# Revit family: EC-25-TY9128_Metric
name_source: partatom
category: Sprinklers
units: mm (PartAtom-declared; Revit-internal decimal feet)

## family parameters
Always vertical = Yes
Cut with Voids When Loaded = No
Maintain Annotation Orientation = No
OmniClass Number = 23.65.70.17.11.24
OmniClass Title = Fire Fighting Sprinkler Heads
Part Type = Normal
Room Calculation Point = No
Round Connector Dimension = Use Diameter
Shared = No
Work Plane-Based = No

## types (2) — shared parameters
COBie = Yes
COBie.Component.Name = Sprinklers:ESFR Upright_SIN
COBie.Type = Yes
COBie.Type.AssetType = Fixed
COBie.Type.Category = Pr_70_55_97_84:Sprinklers
COBie.Type.Colour = Yellow
COBie.Type.DurationUnit = year
COBie.Type.Finish = Natural Brass
COBie.Type.Manufacturer = Tyco Fire Protection Products
COBie.Type.Material = Brass
COBie.Type.Shape = Cylinder
COBie.Type.Size = 1"(DN25)
COBie.Type.WarrantyGuarantorParts = http://tycofsbp.com
Coverage = Standard
Coverage_ = Standard
Finish_ = Natural Brass
K-Factor = 359.5931
Manufacturer = Tyco Fire Protection Products
Manufacturer URL = www.tyco-fire.com
Material_ = Bronze
Model = EC-25
Nominal Diameter 1 = 25 mm
Orifice = Extra Large
Orifice Size = 24 mm
Outside Diameter 1 = 33 mm
Response = Quick
Response_ = Quick
SIN No = TY9128
Takeout 1 = 95 mm
Technical Data Sheet No = TFP213
zero-valued in all types: COBie.Type.NominalHeight, COBie.Type.NominalLength, COBie.Type.NominalWidth, COBie.Type.ReplacementCost, Default Elevation, Style Id

## per-type parameters (varying)
| type | COBie.Component.Description | COBie.Type.ModelNumber | COBie.Type.ModelReference | Description | Part No | Temperature Rating |
| Upright Brass 74°C 25.2K 1" NPT Brass_58-451-1-165 | EC-25 Wet Upright  73.9°C K360 DN25 NPT Br | 58-451-1-165 | EC-25 Wet Upright  73.9°C K360 DN25 NPT Br | EC-25 Upright Brass 74°C 25.2K 1" NPT | 58-451-1-165 | 74 °C |
| Upright Brass 100°C 25.2K 1" NPT Brass_58-451-1-214 | EC-25 Wet Upright  100°C K360 DN25 NPT Br | 58-451-1-214 | EC-25 Wet Upright  100°C K360 DN25 NPT Br | EC-25 Upright Brass 100°C 25.2K 1" NPT | 58-451-1-214 | 100 °C |

## geometry (parser evidence)
native form markers: Blend x2, Sweep x66
no freeform markers — native parametric forms only
